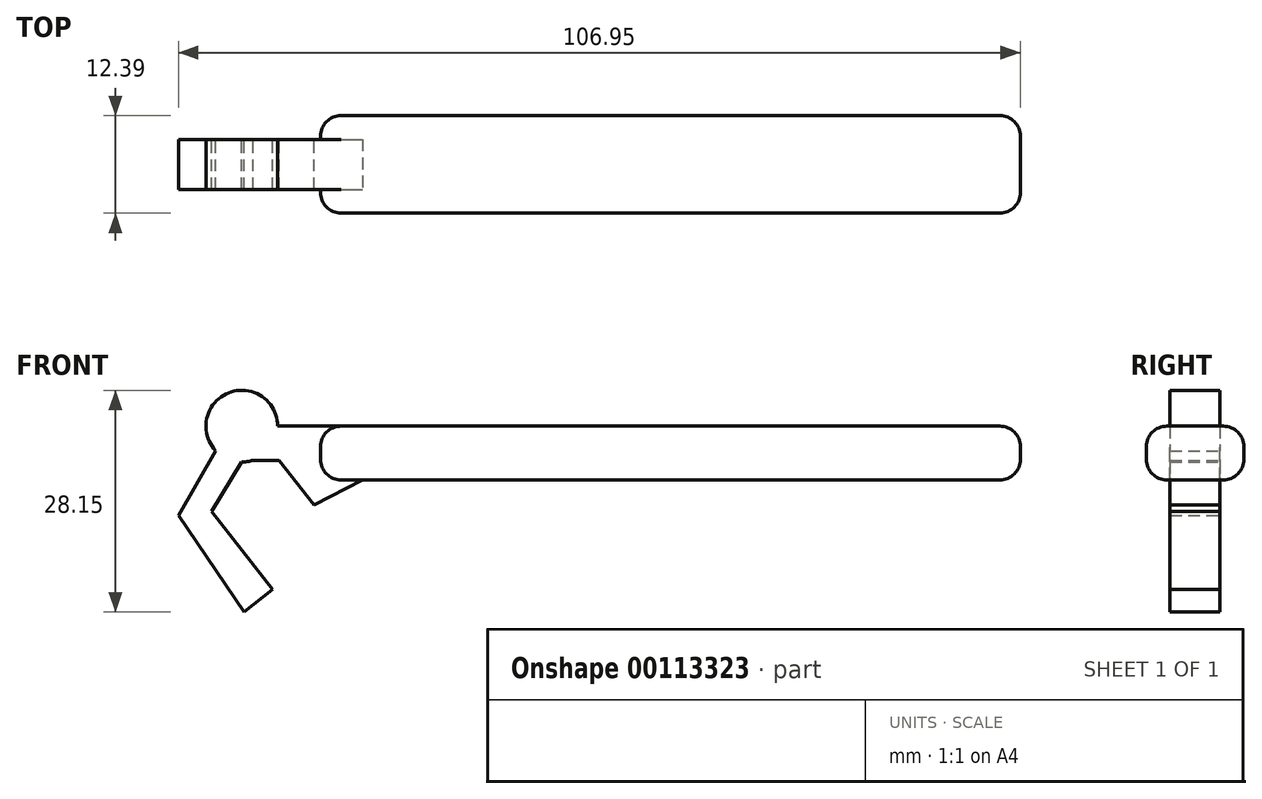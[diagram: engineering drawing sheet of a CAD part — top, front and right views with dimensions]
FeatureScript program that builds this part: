
annotation { "Feature Type Name" : "Feature", "Feature Type Description" : "" }
export const myFeature = defineFeature(function(context is Context, id is Id, definition is map)
    precondition{}
    {
        {
            var Q0;
            Q0=qCreatedBy(makeId("Front.planeOp"),FACE);
            var sketch = newSketch(context, id + "F0", { "sketchPlane" : qUnion([Q0])});
            skLineSegment(sketch, "E0", {"start": v(14.83, 24.83) * mm, "end": v(38.96, 24.83) * mm, "construction": true});
            skCircle(sketch, "E1", {"center": v(14.83, 24.83) * mm, "radius": 3.81 * mm, "construction": true});
            skCircle(sketch, "E2", {"center": v(38.96, 24.83) * mm, "radius": 3.81 * mm, "construction": true});
            skLineSegment(sketch, "E3", {"start": v(14.83, 21.02) * mm, "end": v(38.96, 21.02) * mm, "construction": true});
            skLineSegment(sketch, "E4", {"start": v(38.96, 28.64) * mm, "end": v(14.83, 28.64) * mm, "construction": true});
            skCircle(sketch, "E5", {"center": v(36.65, 33.99) * mm, "radius": 4.56 * mm});
            skLineSegment(sketch, "E6", {"start": v(36.65, 29.43) * mm, "end": v(32.8, 23.17) * mm});
            skLineSegment(sketch, "E7", {"start": v(32.8, 23.17) * mm, "end": v(40.58, 13.26) * mm});
            skLineSegment(sketch, "E8", {"start": v(40.58, 13.26) * mm, "end": v(36.93, 10.4) * mm});
            skLineSegment(sketch, "E9", {"start": v(36.93, 10.4) * mm, "end": v(28.6, 22.64) * mm});
            skLineSegment(sketch, "E10", {"start": v(28.6, 22.64) * mm, "end": v(33.35, 30.86) * mm});
            skLineSegment(sketch, "E11", {"start": v(38.06, 29.65) * mm, "end": v(72.05, 29.65) * mm});
            skLineSegment(sketch, "E12", {"start": v(72.05, 29.65) * mm, "end": v(72.05, 33.99) * mm});
            skLineSegment(sketch, "E13", {"start": v(72.05, 33.99) * mm, "end": v(36.65, 33.99) * mm});
            skLineSegment(sketch, "E14", {"start": v(41.36, 29.65) * mm, "end": v(45.83, 23.97) * mm});
            skLineSegment(sketch, "E15", {"start": v(45.83, 23.97) * mm, "end": v(56.85, 29.65) * mm});
            skSolve(sketch);
        }
        {
            var Q0;
            {var subQ7=sQuery(id+"F0.wireOp",EDGE,"an62Xjg7-xs1e-801o-4J7i-tVXNMO8gq07y");Q0=makeQuery(id+"F0.imprint","IMPRINT",FACE,{"disambiguationData":[TD([[makeQuery(id+"F0.imprint","IMPRINT",EDGE,{"derivedFrom":subQ7}),1.0]])]});}
            var Q1;
            {var subQ0=sQuery(id+"F0.wireOp",EDGE,"ZDsZ1z9R-bY8O-pkCL-OhkM-8RIaMmtdxEmm");var subQ1=makeQuery(id+"F0.imprint","INTERSECT",VERTEX,{"derivedFrom":[subQ0,sQuery(id+"F0.wireOp",EDGE,"PIOQilJV-1L53-h3SG-qBsx-qSoMfwHWGb4X")]});Q1=makeQuery(id+"F0.imprint","IMPRINT",FACE,{"disambiguationData":[TD([[makeQuery(id+"F0.imprint","IMPRINT",EDGE,{"disambiguationData":[TD([[subQ1,1.0]])],"derivedFrom":subQ0}),1.0]])]});}
            var Q2;
            {var subQ0=sQuery(id+"F0.wireOp",EDGE,"I6B12Tz3-ec6J-IiA4-sfc8-q1DKbHCQlqrA");Q2=makeQuery(id+"F0.imprint","IMPRINT",FACE,{"disambiguationData":[TD([[makeQuery(id+"F0.imprint","IMPRINT",EDGE,{"derivedFrom":subQ0}),1.0]])]});}
            var Q3;
            Q3=makeQuery(id+"F0.imprint","IMPRINT",FACE,{"disambiguationData":[TD([[makeQuery(id+"F0.imprint","IMPRINT",EDGE,{"derivedFrom":sQuery(id+"F0.wireOp",EDGE,"WteMS5BJ-g3WS-qfp8-aVoX-5HGdvGbBdg9W")}),1.0]])]});
            var Q4;
            {var subQ0=sQuery(id+"F0.wireOp",EDGE,"E5");var subQ1=makeQuery(id+"F0.imprint","INTERSECT",VERTEX,{"derivedFrom":[subQ0,sQuery(id+"F0.wireOp",EDGE,"E10")]});Q4=makeQuery(id+"F0.imprint","IMPRINT",FACE,{"disambiguationData":[TD([[makeQuery(id+"F0.imprint","IMPRINT",EDGE,{"disambiguationData":[TD([[subQ1,1.0]])],"derivedFrom":subQ0}),1.0]])]});}
            var Q5;
            {var subQ0=sQuery(id+"F0.wireOp",EDGE,"E6");Q5=makeQuery(id+"F0.imprint","IMPRINT",FACE,{"disambiguationData":[TD([[makeQuery(id+"F0.imprint","IMPRINT",EDGE,{"derivedFrom":subQ0}),-1.0]])]});}
            var Q6;
            {var subQ0=sQuery(id+"F0.wireOp",EDGE,"E14");Q6=makeQuery(id+"F0.imprint","IMPRINT",FACE,{"disambiguationData":[TD([[makeQuery(id+"F0.imprint","IMPRINT",EDGE,{"derivedFrom":subQ0}),1.0]])]});}
            var Q7;
            {var subQ0=sQuery(id+"F0.wireOp",EDGE,"E12");Q7=makeQuery(id+"F0.imprint","IMPRINT",FACE,{"disambiguationData":[TD([[makeQuery(id+"F0.imprint","IMPRINT",EDGE,{"derivedFrom":subQ0}),1.0]])]});}
            extrude(context, id + "F1", {"entities" : qUnion([Q0, Q1, Q2, Q3, Q4, Q5, Q6, Q7]), "depth" : 6.35 * mm});
        }
        {
            var Q0;
            Q0=makeQuery(id+"F1.opExtrude","SWEPT_FACE",FACE,{"disambiguationData":[OSD([sQuery(id+"F0.wireOp",EDGE,"E12")])]});
            var sketch = newSketch(context, id + "F2", { "sketchPlane" : qUnion([Q0])});
            skLineSegment(sketch, "E16", {"start": v(-6.35, 33.99) * mm, "end": v(-9.37, 33.99) * mm});
            skLineSegment(sketch, "E17", {"start": v(-9.37, 33.99) * mm, "end": v(-9.37, 27.17) * mm});
            skLineSegment(sketch, "E18", {"start": v(-9.37, 27.17) * mm, "end": v(3.02, 27.17) * mm});
            skLineSegment(sketch, "E19", {"start": v(3.02, 27.17) * mm, "end": v(3.02, 33.99) * mm});
            skLineSegment(sketch, "E20", {"start": v(3.02, 33.99) * mm, "end": v(0, 33.99) * mm});
            skSolve(sketch);
        }
        {
            var Q0;
            Q0=makeQuery(id+"F2.imprint","IMPRINT",FACE,{"disambiguationData":[TD([[makeQuery(id+"F2.imprint","IMPRINT",EDGE,{"derivedFrom":sQuery(id+"F2.wireOp",EDGE,"E16")}),1.0]])]});
            var Q1;
            {var subQ0=sQuery(id+"F0.wireOp",EDGE,"E12");Q1=makeQuery(id+"F2.imprint","IMPRINT",FACE,{"disambiguationData":[TD([[makeQuery(id+"F2.imprint","IMPRINT",EDGE,{"derivedFrom":makeQuery(id+"F1.opExtrude","CAP_EDGE",EDGE,{"disambiguationData":[OSD([subQ0])],"isStart":true})}),1.0]])]});}
            extrude(context, id + "F3", {"entities" : qUnion([Q0, Q1]), "operationType" : NewBodyOperationType.ADD, "oppositeDirection" : true, "depth" : 25.4 * mm});
        }
        {
            var Q0;
            {var subQ0=sQuery(id+"F0.wireOp",EDGE,"E12");Q0=makeQuery(id+"F3.boolean.opBoolean","MERGE",FACE,{"derivedFrom":[makeQuery(id+"F1.opExtrude","SWEPT_FACE",FACE,{"disambiguationData":[OSD([subQ0])]}),makeQuery(id+"F3.opExtrude","CAP_FACE",FACE,{"disambiguationData":[OSD([subQ0,sQuery(id+"F0.wireOp",EDGE,"E13"),sQuery(id+"F2.wireOp",EDGE,"E16"),sQuery(id+"F2.wireOp",EDGE,"E17"),sQuery(id+"F2.wireOp",EDGE,"E18"),sQuery(id+"F2.wireOp",EDGE,"E19"),sQuery(id+"F2.wireOp",EDGE,"E20")])],"isStart":true})]});}
            extrude(context, id + "F4", {"entities" : qUnion([Q0]), "operationType" : NewBodyOperationType.ADD, "depth" : 63.5 * mm});
        }
        {
            var Q0;
            {var subQ0=sQuery(id+"F2.wireOp",EDGE,"E20");var subQ1=sQuery(id+"F2.wireOp",EDGE,"E19");Q0=makeQuery(id+"F4.boolean.opBoolean","MERGE",EDGE,{"derivedFrom":[makeQuery(id+"F3.opExtrude","SWEPT_EDGE",EDGE,{"disambiguationData":[OSD([subQ1,subQ0])]}),makeQuery(id+"F4.opExtrude","SWEPT_EDGE",EDGE,{"disambiguationData":[OSD([subQ1,subQ0])]})]});}
            var Q1;
            {var subQ0=sQuery(id+"F2.wireOp",EDGE,"E19");var subQ1=sQuery(id+"F2.wireOp",EDGE,"E18");Q1=makeQuery(id+"F4.boolean.opBoolean","MERGE",EDGE,{"derivedFrom":[makeQuery(id+"F3.opExtrude","SWEPT_EDGE",EDGE,{"disambiguationData":[OSD([subQ1,subQ0])]}),makeQuery(id+"F4.opExtrude","SWEPT_EDGE",EDGE,{"disambiguationData":[OSD([subQ1,subQ0])]})]});}
            var Q2;
            {var subQ0=sQuery(id+"F2.wireOp",EDGE,"E18");var subQ1=sQuery(id+"F2.wireOp",EDGE,"E17");Q2=makeQuery(id+"F4.boolean.opBoolean","MERGE",EDGE,{"derivedFrom":[makeQuery(id+"F3.opExtrude","SWEPT_EDGE",EDGE,{"disambiguationData":[OSD([subQ1,subQ0])]}),makeQuery(id+"F4.opExtrude","SWEPT_EDGE",EDGE,{"disambiguationData":[OSD([subQ1,subQ0])]})]});}
            var Q3;
            {var subQ0=sQuery(id+"F2.wireOp",EDGE,"E17");var subQ1=sQuery(id+"F2.wireOp",EDGE,"E16");Q3=makeQuery(id+"F4.boolean.opBoolean","MERGE",EDGE,{"derivedFrom":[makeQuery(id+"F3.opExtrude","SWEPT_EDGE",EDGE,{"disambiguationData":[OSD([subQ1,subQ0])]}),makeQuery(id+"F4.opExtrude","SWEPT_EDGE",EDGE,{"disambiguationData":[OSD([subQ1,subQ0])]})]});}
            var Q4;
            Q4=makeQuery(id+"F4.opExtrude","CAP_EDGE",EDGE,{"disambiguationData":[OSD([sQuery(id+"F0.wireOp",EDGE,"E12"),sQuery(id+"F0.wireOp",EDGE,"E13"),sQuery(id+"F2.wireOp",EDGE,"E16"),sQuery(id+"F2.wireOp",EDGE,"E20")])],"isStart":false});
            var Q5;
            Q5=makeQuery(id+"F4.opExtrude","CAP_EDGE",EDGE,{"disambiguationData":[OSD([sQuery(id+"F2.wireOp",EDGE,"E18")])],"isStart":false});
            var Q6;
            Q6=makeQuery(id+"F4.opExtrude","CAP_EDGE",EDGE,{"disambiguationData":[OSD([sQuery(id+"F2.wireOp",EDGE,"E17")])],"isStart":false});
            var Q7;
            Q7=makeQuery(id+"F4.opExtrude","CAP_EDGE",EDGE,{"disambiguationData":[OSD([sQuery(id+"F2.wireOp",EDGE,"E19")])],"isStart":false});
            var Q8;
            Q8=makeQuery(id+"F3.opExtrude","CAP_EDGE",EDGE,{"disambiguationData":[OSD([sQuery(id+"F2.wireOp",EDGE,"E19")])],"isStart":false});
            var Q9;
            {var subQ0=sQuery(id+"F0.wireOp",EDGE,"E13");var subQ1=sQuery(id+"F2.wireOp",EDGE,"E20");var subQ2=sQuery(id+"F2.wireOp",EDGE,"E16");var subQ3=sQuery(id+"F0.wireOp",EDGE,"E12");var subQ4=sQuery(id+"F2.wireOp",EDGE,"E19");Q9=makeQuery(id+"F3.boolean.opBoolean","SPLIT",EDGE,{"disambiguationData":[TD([makeQuery(id+"F3.opExtrude","SWEPT_FACE",FACE,{"disambiguationData":[OSD([subQ4])]})])],"derivedFrom":makeQuery(id+"F3.opExtrude","CAP_EDGE",EDGE,{"disambiguationData":[OSD([subQ3,subQ0,subQ2,subQ1])],"isStart":false})});}
            var Q10;
            {var subQ2=sQuery(id+"F2.wireOp",EDGE,"E19");var subQ3=sQuery(id+"F2.wireOp",EDGE,"E18");Q10=makeQuery(id+"F3.boolean.opBoolean","SPLIT",EDGE,{"disambiguationData":[TD([makeQuery(id+"F3.opExtrude","SWEPT_FACE",FACE,{"disambiguationData":[OSD([subQ2])]})])],"derivedFrom":makeQuery(id+"F3.opExtrude","CAP_EDGE",EDGE,{"disambiguationData":[OSD([subQ3])],"isStart":false})});}
            var Q11;
            {var subQ0=sQuery(id+"F2.wireOp",EDGE,"E20");var subQ1=sQuery(id+"F2.wireOp",EDGE,"E16");var subQ2=sQuery(id+"F0.wireOp",EDGE,"E13");var subQ3=sQuery(id+"F0.wireOp",EDGE,"E12");var subQ4=sQuery(id+"F2.wireOp",EDGE,"E17");Q11=makeQuery(id+"F3.boolean.opBoolean","SPLIT",EDGE,{"disambiguationData":[TD([makeQuery(id+"F3.opExtrude","SWEPT_FACE",FACE,{"disambiguationData":[OSD([subQ4])]})])],"derivedFrom":makeQuery(id+"F3.opExtrude","CAP_EDGE",EDGE,{"disambiguationData":[OSD([subQ3,subQ2,subQ1,subQ0])],"isStart":false})});}
            var Q12;
            {var subQ2=sQuery(id+"F2.wireOp",EDGE,"E18");var subQ3=sQuery(id+"F2.wireOp",EDGE,"E17");Q12=makeQuery(id+"F3.boolean.opBoolean","SPLIT",EDGE,{"disambiguationData":[TD([makeQuery(id+"F3.opExtrude","SWEPT_FACE",FACE,{"disambiguationData":[OSD([subQ3])]})])],"derivedFrom":makeQuery(id+"F3.opExtrude","CAP_EDGE",EDGE,{"disambiguationData":[OSD([subQ2])],"isStart":false})});}
            var Q13;
            Q13=makeQuery(id+"F3.opExtrude","CAP_EDGE",EDGE,{"disambiguationData":[OSD([sQuery(id+"F2.wireOp",EDGE,"E17")])],"isStart":false});
            fillet(context, id + "F5", {"entities" : qUnion([Q0, Q1, Q2, Q3, Q4, Q5, Q6, Q7, Q8, Q9, Q10, Q11, Q12, Q13]), "radius" : 2.6 * mm, "tangentPropagation" : true, "allowEdgeOverflow" : false});
        }
    });
